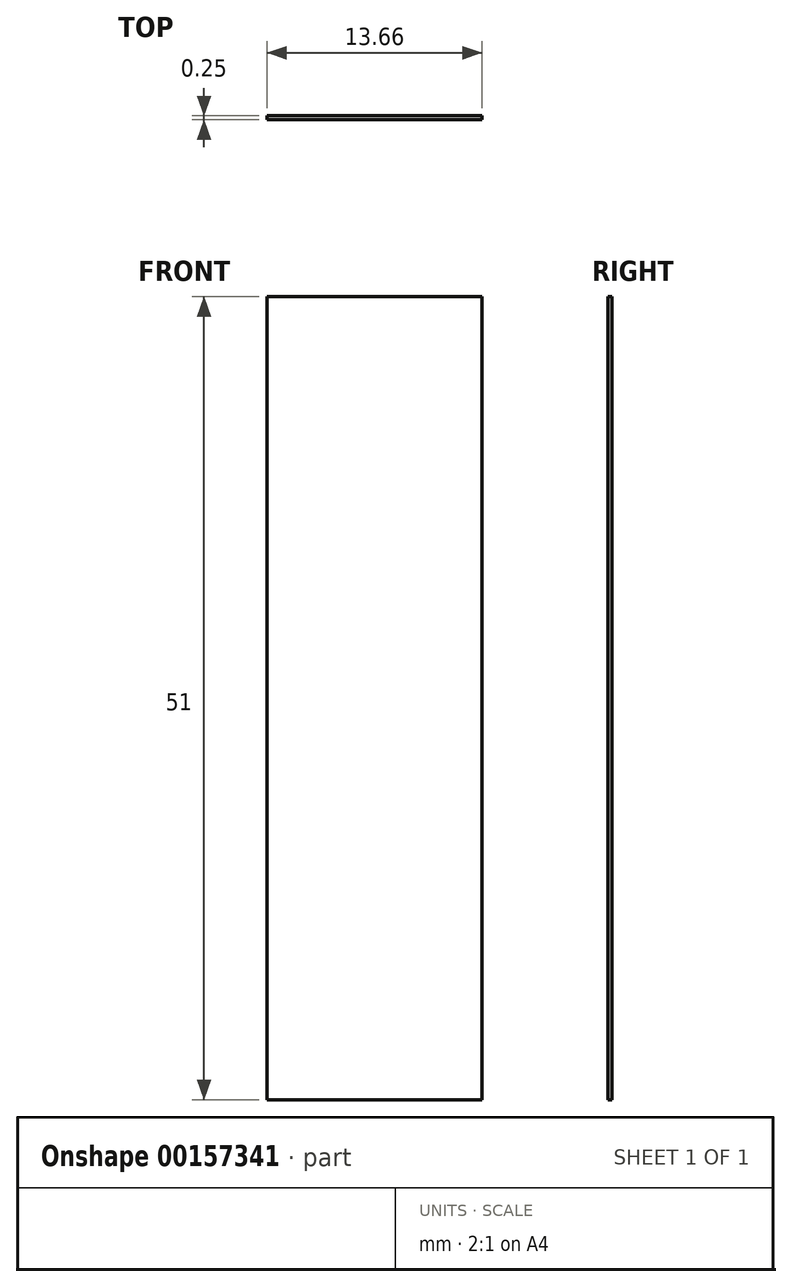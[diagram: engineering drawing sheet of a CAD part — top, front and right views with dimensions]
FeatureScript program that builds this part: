
annotation { "Feature Type Name" : "Feature", "Feature Type Description" : "" }
export const myFeature = defineFeature(function(context is Context, id is Id, definition is map)
    precondition{}
    {
        {
            var Q0;
            Q0=qCreatedBy(makeId("Front.planeOp"),FACE);
            var sketch = newSketch(context, id + "F0", { "sketchPlane" : qUnion([Q0])});
            skLineSegment(sketch, "E0.bottom", {"start": v(6.83, 25.5) * mm, "end": v(-6.82, 25.5) * mm});
            skLineSegment(sketch, "E0.top", {"start": v(6.83, -25.5) * mm, "end": v(-6.83, -25.5) * mm});
            skLineSegment(sketch, "E0.left", {"start": v(6.83, 25.5) * mm, "end": v(6.83, -25.5) * mm});
            skLineSegment(sketch, "E0.right", {"start": v(-6.82, 25.5) * mm, "end": v(-6.83, -25.5) * mm});
            skPoint(sketch, "E0.middle", {"position": v(0, 0) * mm});
            skSolve(sketch);
        }
        {
            var Q0;
            Q0=makeQuery(id+"F0.imprint","IMPRINT",FACE,{"disambiguationData":[TD([[makeQuery(id+"F0.imprint","IMPRINT",EDGE,{"derivedFrom":sQuery(id+"F0.wireOp",EDGE,"E0.bottom")}),1.0]])]});
            extrude(context, id + "F1", {"entities" : qUnion([Q0]), "depth" : 0.25 * mm});
        }
    });
